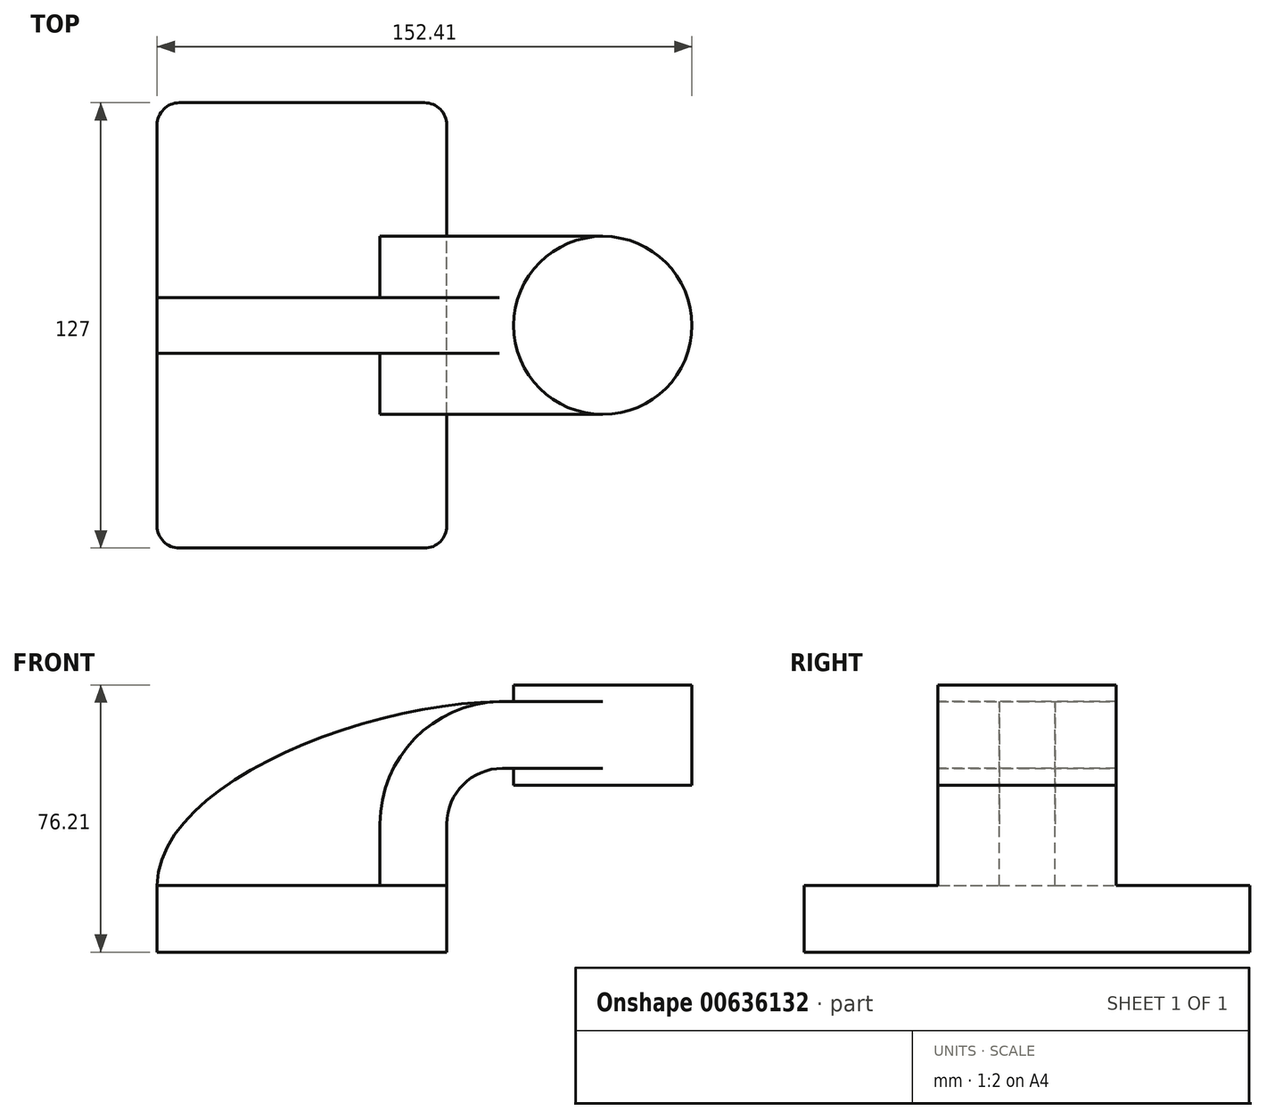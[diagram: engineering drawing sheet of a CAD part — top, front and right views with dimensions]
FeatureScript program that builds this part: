
annotation { "Feature Type Name" : "Feature", "Feature Type Description" : "" }
export const myFeature = defineFeature(function(context is Context, id is Id, definition is map)
    precondition{}
    {
        {
            var Q0;
            Q0=qCreatedBy(makeId("Front.planeOp"),FACE);
            var sketch = newSketch(context, id + "F0", { "sketchPlane" : qUnion([Q0])});
            skLineSegment(sketch, "E0.bottom", {"start": v(41.28, -9.52) * mm, "end": v(-41.28, -9.53) * mm});
            skLineSegment(sketch, "E0.top", {"start": v(41.28, 9.53) * mm, "end": v(-41.28, 9.53) * mm});
            skLineSegment(sketch, "E0.left", {"start": v(41.28, -9.52) * mm, "end": v(41.28, 9.53) * mm});
            skLineSegment(sketch, "E0.right", {"start": v(-41.28, -9.53) * mm, "end": v(-41.28, 9.53) * mm});
            skPoint(sketch, "E0.middle", {"position": v(0, 0) * mm});
            skPoint(sketch, "E1.middle", {"position": v(85.72, 52.39) * mm});
            skLineSegment(sketch, "E2", {"start": v(41.28, 9.53) * mm, "end": v(41.28, 27) * mm});
            skArc(sketch, "E3", {"start": v(41.27, 27) * mm, "mid": v(45.92, 38.23) * mm, "end": v(57.15, 42.88) * mm});
            skArc(sketch, "E4.1", {"start": v(22.23, 27) * mm, "mid": v(32.45, 51.7) * mm, "end": v(57.15, 61.93) * mm});
            skLineSegment(sketch, "E4.2", {"start": v(22.22, 9.53) * mm, "end": v(22.22, 27) * mm});
            skFitSpline(sketch, "E5", {"points": [v(-41.28, 9.53) * mm, v(57.15, 61.93) * mm], "startDerivative": vector(0.9, 86.74) * mm, "endDerivative": vector(119.32, 1.08) * mm});
            skLineSegment(sketch, "E6", {"start": v(57.15, 42.88) * mm, "end": v(85.72, 42.88) * mm});
            skLineSegment(sketch, "E7", {"start": v(57.15, 61.93) * mm, "end": v(85.72, 61.93) * mm});
            skLineSegment(sketch, "E8.bottom", {"start": v(111.12, 38.1) * mm, "end": v(60.32, 38.1) * mm});
            skLineSegment(sketch, "E8.top", {"start": v(111.12, 66.68) * mm, "end": v(60.32, 66.68) * mm});
            skLineSegment(sketch, "E8.left", {"start": v(111.12, 38.1) * mm, "end": v(111.12, 66.68) * mm});
            skLineSegment(sketch, "E8.right", {"start": v(60.32, 38.1) * mm, "end": v(60.32, 66.68) * mm});
            skLineSegment(sketch, "E9", {"start": v(85.72, 38.1) * mm, "end": v(85.72, 66.68) * mm});
            skSolve(sketch);
        }
        {
            var Q0;
            Q0=makeQuery(id+"F0.imprint","IMPRINT",FACE,{"disambiguationData":[TD([[makeQuery(id+"F0.imprint","IMPRINT",EDGE,{"derivedFrom":sQuery(id+"F0.wireOp",EDGE,"E0.bottom")}),-1.0]])]});
            extrude(context, id + "F1", {"entities" : qUnion([Q0]), "endBound" : BoundingType.SYMMETRIC, "depth" : 127 * mm, "offsetDistance" : 25.4 * mm});
        }
        {
            var Q0;
            {var subQ4=sQuery(id+"F0.wireOp",EDGE,"E2");Q0=makeQuery(id+"F0.imprint","IMPRINT",FACE,{"disambiguationData":[TD([[makeQuery(id+"F0.imprint","IMPRINT",EDGE,{"derivedFrom":subQ4}),1.0]])]});}
            var Q1;
            {var subQ0=sQuery(id+"F0.wireOp",EDGE,"E9");var subQ1=sQuery(id+"F0.wireOp",EDGE,"E6");var subQ2=makeQuery(id+"F0.imprint","INTERSECT",VERTEX,{"derivedFrom":[subQ1,subQ0]});Q1=makeQuery(id+"F0.imprint","IMPRINT",FACE,{"disambiguationData":[TD([[makeQuery(id+"F0.imprint","IMPRINT",EDGE,{"disambiguationData":[TD([[subQ2,1.0]])],"derivedFrom":subQ1}),1.0]])]});}
            extrude(context, id + "F2", {"entities" : qUnion([Q0, Q1]), "endBound" : BoundingType.SYMMETRIC, "depth" : 50.8 * mm, "offsetDistance" : 25.4 * mm});
        }
        {
            var Q0;
            {var subQ3=sQuery(id+"F0.wireOp",EDGE,"E4.2");Q0=makeQuery(id+"F0.imprint","IMPRINT",FACE,{"disambiguationData":[TD([[makeQuery(id+"F0.imprint","IMPRINT",EDGE,{"derivedFrom":subQ3}),1.0]])]});}
            extrude(context, id + "F3", {"entities" : qUnion([Q0]), "operationType" : NewBodyOperationType.ADD, "endBound" : BoundingType.SYMMETRIC, "depth" : 15.88 * mm, "offsetDistance" : 25.4 * mm});
        }
        {
            var Q0;
            {var subQ4=sQuery(id+"F0.wireOp",EDGE,"E8.left");Q0=makeQuery(id+"F0.imprint","IMPRINT",FACE,{"disambiguationData":[TD([[makeQuery(id+"F0.imprint","IMPRINT",EDGE,{"derivedFrom":subQ4}),1.0]])]});}
            var Q1;
            Q1=sQuery(id+"F0.wireOp",EDGE,"E9");
            revolve(context, id + "F4", {"operationType" : NewBodyOperationType.ADD, "entities" : qUnion([Q0]), "axis" : qUnion([Q1]), "revolveType" : RevolveType.FULL});
        }
        {
            var Q0;
            Q0=makeQuery(id+"F1.opExtrude","CAP_EDGE",EDGE,{"disambiguationData":[OSD([sQuery(id+"F0.wireOp",EDGE,"E0.left")])],"isStart":false});
            var Q1;
            Q1=makeQuery(id+"F1.opExtrude","CAP_EDGE",EDGE,{"disambiguationData":[OSD([sQuery(id+"F0.wireOp",EDGE,"E0.right")])],"isStart":false});
            var Q2;
            Q2=makeQuery(id+"F1.opExtrude","CAP_EDGE",EDGE,{"disambiguationData":[OSD([sQuery(id+"F0.wireOp",EDGE,"E0.left")])],"isStart":true});
            var Q3;
            Q3=makeQuery(id+"F1.opExtrude","CAP_EDGE",EDGE,{"disambiguationData":[OSD([sQuery(id+"F0.wireOp",EDGE,"E0.right")])],"isStart":true});
            fillet(context, id + "F5", {"entities" : qUnion([Q0, Q1, Q2, Q3]), "radius" : 6.35 * mm, "tangentPropagation" : true, "allowEdgeOverflow" : false});
        }
    });
